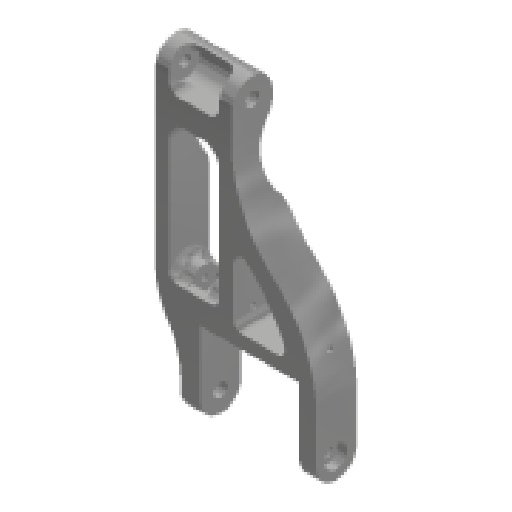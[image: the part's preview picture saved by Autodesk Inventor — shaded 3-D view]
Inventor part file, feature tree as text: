
AUTODESK INVENTOR PART (.ipt)
format: ipt  version: 2025 (Build 290162000, 162)  size: 483,840 bytes
history: native  units: in
note: dims shown in document units (in); Inventor stores cm internally (conversion verified against a paired STEP export)
features: extrude x15, sketch x15, projected_geometry x13, fillet x11, plane x4, other x3, mirror x2, reference x1
ambient origin geometry x8: Origin, YZ Plane, XZ Plane, XY Plane, X Axis, Y Axis, Z Axis, Center Point
bodies: Solid1 (feature_tree)
feature tree (64):
  extrude  "Extrusion1"  Depth=0.315in TaperAngle=0.0deg
  extrude  "Extrusion2"  Depth=0.2559in
  extrude  "Extrusion3"  Depth=0.1181in
  plane  "Work Plane1"
  mirror  "Mirror1"
  extrude  "Extrusion4"  Depth=0.315in TaperAngle=0.0deg
  extrude  "Extrusion5"  Depth=0.5in
  fillet  "Fillet1"  Radius=1.0in
  extrude  "Extrusion6"  Depth=0.25in
  fillet  "Fillet2"  [1 undecoded]
  fillet  "Fillet4"  Radius=0.3228in
  plane  "Work Plane2"
  extrude  "Extrusion7"  Depth=1.5in
  fillet  "Fillet5"  Radius=0.2362in
  extrude  "Extrusion8"  Depth=0.3937in
  fillet  "Fillet6"  Radius=0.3937in
  extrude  "Extrusion9"  Depth=0.3937in TaperAngle=0.0deg
  mirror  "Mirror2"
  fillet  "Fillet7"  Radius=1.5507in
  sketch  "Sketch10"  dims[d38=0.4724in d39=0.0in d40=3.0in]
  plane  "Work Plane3"
  extrude  "Extrusion10"  Depth=3.0in
  sketch  "Sketch11"  dims[d41=0.2362in d42=0.0in d43=0.0in d44=0.0in]
  plane  "Work Plane4"
  extrude  "Extrusion11"  TaperAngle=0.0deg  [1 undecoded]
  extrude  "Extrusion12"  Depth=0.5087in
  fillet  "Fillet8"  Radius=0.1969in
  extrude  "Extrusion13"  Depth=0.25in
  extrude  "Extrusion14"  TaperAngle=0.0deg  [1 undecoded]
  fillet  "Fillet9"  [1 undecoded]
  fillet  "Fillet10"  [1 undecoded]
  fillet  "Fillet12"  [1 undecoded]
  fillet  "Fillet13"  [1 undecoded]
  extrude  "Extrusion15"  [1 undecoded]
  sketch  "Sketch1"  dims[d0=0.3346in d1=0.315in d2=0.0in]
  sketch  "Sketch2"  dims[d3=0.0787in d4=0.0in d5=0.2559in]
  projected_geometry  "Projected Loop1"
  sketch  "Sketch3"  dims[d6=0.1181in d7=0.0in d8=0.1181in]
  projected_geometry  "Projected Loop2"
  sketch  "Sketch4"  dims[d9=0.6102in d10=0.315in d11=0.0in]
  projected_geometry  "Projected Loop3"
  sketch  "Sketch5"  dims[d12=0.0in d13=0.0in d14=0.5in d15=1.0in d16=0.0in]
  projected_geometry  "Projected Loop4"
  sketch  "Sketch6"  dims[d17=0.25in d19=0.4in d20=-1.0836in d21=0.3228in]
  projected_geometry  "Projected Loop5"
  sketch  "Sketch7"  dims[d22=0.4724in d23=0.0in d24=1.5in d25=0.2362in]
  projected_geometry  "Projected Loop6"
  reference  "Reference1"
  sketch  "Sketch8"  dims[d26=0.1575in d27=0.0in d28=2.0in d29=0.3937in d30=0.0in]
  sketch  "Sketch9"  dims[d31=0.25in d33=-0.2362in d34=0.3937in d35=0.0in d36=1.5507in d37=0.0in]
  projected_geometry  "Projected Loop7"
  projected_geometry  "Projected Loop8"
  projected_geometry  "Projected Loop9"
  sketch  "Sketch12"  dims[d45=0.1969in d46=0.5087in d47=0.1969in]
  projected_geometry  "Projected Loop10"
  projected_geometry  "Projected Loop11"
  sketch  "Sketch13"  dims[d49=0.25in d50=0.25in]
  sketch  "Sketch14"  dims[d51=0.0591in d52=0.0in d48=0.0in]
  projected_geometry  "Projected Loop12"
  sketch  "Sketch15"
  projected_geometry  "Projected Loop13"
  other  "<userpath>\Desktop\puppycat\singleSwingarmV2.iam"
  other  "singleSwingarmV2.iam"
  other  "6082rsBearing:3"
note: 8 required parameter values undecoded (feature->parameter linkage not recoverable at this tier; creation-order binding heuristic only, values carry confidence <= 0.55)
